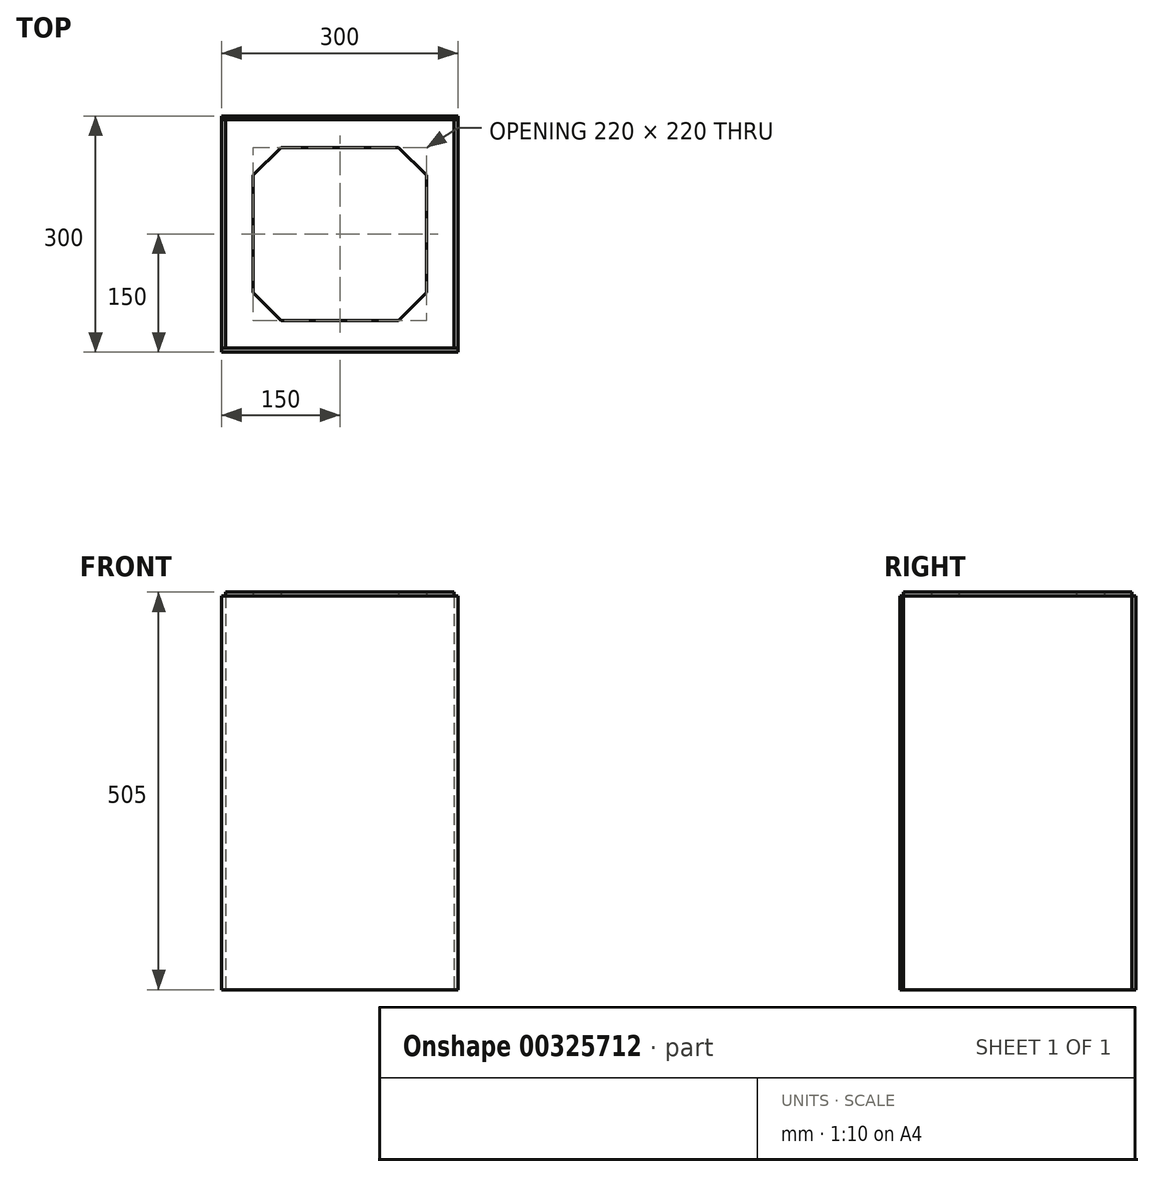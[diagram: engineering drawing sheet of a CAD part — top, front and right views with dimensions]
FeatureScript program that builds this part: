
annotation { "Feature Type Name" : "Feature", "Feature Type Description" : "" }
export const myFeature = defineFeature(function(context is Context, id is Id, definition is map)
    precondition{}
    {
        {
            assignVariable(context, id + "F0", {"name" : "ALTO", "anyValue" : 500});
        }
        {
            assignVariable(context, id + "F1", {"name" : "ESPESOR", "anyValue" : 5});
        }
        {
            var Q0;
            Q0=qCreatedBy(makeId("Top.planeOp"),FACE);
            var sketch = newSketch(context, id + "F2", { "sketchPlane" : qUnion([Q0])});
            skLineSegment(sketch, "E0.bottom", {"start": v(0, 0) * mm, "end": v(300, 0) * mm});
            skLineSegment(sketch, "E0.top", {"start": v(0, 300) * mm, "end": v(300, 300) * mm});
            skLineSegment(sketch, "E0.left", {"start": v(0, 0) * mm, "end": v(0, 300) * mm});
            skLineSegment(sketch, "E0.right", {"start": v(300, 0) * mm, "end": v(300, 300) * mm});
            skLineSegment(sketch, "E1.0", {"start": v(5, 295) * mm, "end": v(295, 295) * mm});
            skLineSegment(sketch, "E1.1", {"start": v(5, 5) * mm, "end": v(5, 295) * mm});
            skLineSegment(sketch, "E1.2", {"start": v(5, 5) * mm, "end": v(295, 5) * mm});
            skLineSegment(sketch, "E1.3", {"start": v(295, 5) * mm, "end": v(295, 295) * mm});
            skLineSegment(sketch, "E2", {"start": v(0, 295) * mm, "end": v(300, 295) * mm});
            skLineSegment(sketch, "E3", {"start": v(0, 5) * mm, "end": v(300, 5) * mm});
            skLineSegment(sketch, "E4.0", {"start": v(40, 260) * mm, "end": v(260, 260) * mm});
            skLineSegment(sketch, "E4.1", {"start": v(40, 40) * mm, "end": v(40, 260) * mm});
            skLineSegment(sketch, "E4.2", {"start": v(40, 40) * mm, "end": v(260, 40) * mm});
            skLineSegment(sketch, "E4.3", {"start": v(260, 40) * mm, "end": v(260, 260) * mm});
            skLineSegment(sketch, "E5", {"start": v(40, 224.64) * mm, "end": v(75.36, 260) * mm});
            skLineSegment(sketch, "E6", {"start": v(150, 344.95) * mm, "end": v(150, 390.38) * mm, "construction": true});
            skPoint(sketch, "E6.startSnap0", {"position": v(150, 300) * mm});
            skLineSegment(sketch, "E7", {"start": v(329.89, 150) * mm, "end": v(483.12, 150) * mm, "construction": true});
            skPoint(sketch, "E7.startSnap0", {"position": v(300, 150) * mm});
            skPoint(sketch, "E7.endSnap0", {"position": v(300, 150) * mm});
            skLineSegment(sketch, "E8.MirrorCS", {"start": v(260, 224.64) * mm, "end": v(224.64, 260) * mm});
            skLineSegment(sketch, "E9.MirrorCS", {"start": v(260, 75.36) * mm, "end": v(224.64, 40) * mm});
            skLineSegment(sketch, "E10.MirrorCS", {"start": v(40, 75.36) * mm, "end": v(75.36, 40) * mm});
            skSolve(sketch);
        }
        {
            var Q0;
            {var subQ5=sQuery(id+"F2.wireOp",EDGE,"E0.top");Q0=makeQuery(id+"F2.imprint","IMPRINT",FACE,{"disambiguationData":[TD([[makeQuery(id+"F2.imprint","IMPRINT",EDGE,{"derivedFrom":subQ5}),-1.0]])]});}
            var Q1;
            {var subQ4=sQuery(id+"F2.wireOp",EDGE,"E0.bottom");Q1=makeQuery(id+"F2.imprint","IMPRINT",FACE,{"disambiguationData":[TD([[makeQuery(id+"F2.imprint","IMPRINT",EDGE,{"derivedFrom":subQ4}),1.0]])]});}
            extrude(context, id + "F3", {"entities" : qUnion([Q0, Q1]), "depth" : (getVariable(context, 'ALTO')) * mm});
        }
        {
            var Q0;
            {var subQ5=sQuery(id+"F2.wireOp",EDGE,"E1.1");Q0=makeQuery(id+"F2.imprint","IMPRINT",FACE,{"disambiguationData":[TD([[makeQuery(id+"F2.imprint","IMPRINT",EDGE,{"derivedFrom":subQ5}),1.0]])]});}
            var Q1;
            {var subQ5=sQuery(id+"F2.wireOp",EDGE,"E1.3");Q1=makeQuery(id+"F2.imprint","IMPRINT",FACE,{"disambiguationData":[TD([[makeQuery(id+"F2.imprint","IMPRINT",EDGE,{"derivedFrom":subQ5}),-1.0]])]});}
            extrude(context, id + "F4", {"entities" : qUnion([Q0, Q1]), "depth" : (getVariable(context, 'ALTO')) * mm});
        }
        {
            var Q0;
            {var subQ14=sQuery(id+"F2.wireOp",EDGE,"E1.1");Q0=makeQuery(id+"F2.imprint","IMPRINT",FACE,{"disambiguationData":[TD([[makeQuery(id+"F2.imprint","IMPRINT",EDGE,{"derivedFrom":subQ14}),-1.0]])]});}
            var Q1;
            {var subQ3=sQuery(id+"F2.wireOp",EDGE,"E8.MirrorCS");Q1=makeQuery(id+"F2.imprint","IMPRINT",FACE,{"disambiguationData":[TD([[makeQuery(id+"F2.imprint","IMPRINT",EDGE,{"derivedFrom":subQ3}),-1.0]])]});}
            var Q2;
            {var subQ3=sQuery(id+"F2.wireOp",EDGE,"E5");Q2=makeQuery(id+"F2.imprint","IMPRINT",FACE,{"disambiguationData":[TD([[makeQuery(id+"F2.imprint","IMPRINT",EDGE,{"derivedFrom":subQ3}),1.0]])]});}
            var Q3;
            {var subQ3=sQuery(id+"F2.wireOp",EDGE,"E10.MirrorCS");Q3=makeQuery(id+"F2.imprint","IMPRINT",FACE,{"disambiguationData":[TD([[makeQuery(id+"F2.imprint","IMPRINT",EDGE,{"derivedFrom":subQ3}),-1.0]])]});}
            var Q4;
            {var subQ3=sQuery(id+"F2.wireOp",EDGE,"E9.MirrorCS");Q4=makeQuery(id+"F2.imprint","IMPRINT",FACE,{"disambiguationData":[TD([[makeQuery(id+"F2.imprint","IMPRINT",EDGE,{"derivedFrom":subQ3}),1.0]])]});}
            extrude(context, id + "F5", {"entities" : qUnion([Q0, Q1, Q2, Q3, Q4]), "depth" : (getVariable(context, 'ALTO') + getVariable(context, 'ESPESOR')) * mm, "hasSecondDirection" : true, "secondDirectionOppositeDirection" : false, "secondDirectionDepth" : (getVariable(context, 'ALTO')) * mm});
        }
    });
